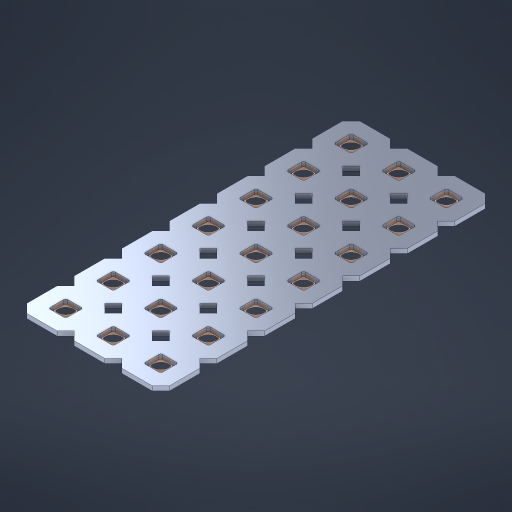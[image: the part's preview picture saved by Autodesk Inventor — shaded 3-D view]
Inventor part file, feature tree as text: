
AUTODESK INVENTOR PART (.ipt)
format: ipt  version: 2023 (Build 270158000, 158)  size: 497,664 bytes
history: native  units: in
note: dims shown in document units (in); Inventor stores cm internally (conversion verified against a paired STEP export)
features: other x22, extrude x20, sketch x2, pattern_linear x1
ambient origin geometry x8: Origin, YZ Plane, XZ Plane, XY Plane, X Axis, Y Axis, Z Axis, Center Point
bodies: Solid1 (feature_tree), Body (feature_tree)
feature tree (45):
  pattern_linear  "Rectangular Pattern1"  Spacing1=0.09in  [1 undecoded]
  sketch  "Sketch1"  dims[d1=0.5in]
  sketch  "Sketch2"  dims[d2=0.182in d3=0.09in d4=0.09in d5=0.09in d6=0.09in d7=0.09in d8=0.09in d9=0.09in d10=0.09in d11=0.02in d13=0.0in d14=0.172in d15=0.0625in d16=0.0in d19=0.5in d22=0.5in]
  other  "Srf1"
  other  "Srf126"
  other  "Srf127"
  other  "Srf128"
  other  "Srf129"
  other  "Srf130"
  other  "Srf131"
  other  "Srf268"
  other  "Srf269"
  other  "Srf270"
  other  "Srf271"
  other  "Srf272"
  other  "Srf273"
  other  "Srf274"
  other  "Srf293"
  other  "Srf294"
  other  "Srf295"
  other  "Srf296"
  other  "Srf297"
  other  "Srf298"
  other  "Srf299"
  other  "Circle"
  extrude  "ExtrusionSrf126"  Depth=0.09in
  extrude  "ExtrusionSrf127"  Depth=0.09in
  extrude  "ExtrusionSrf128"  Depth=0.09in
  extrude  "ExtrusionSrf129"  Depth=0.09in
  extrude  "ExtrusionSrf130"  Depth=0.09in
  extrude  "ExtrusionSrf131"  Depth=0.09in
  extrude  "ExtrusionSrf268"  Depth=0.09in
  extrude  "ExtrusionSrf269"  Depth=0.02in
  extrude  "ExtrusionSrf270"  TaperAngle=0.0deg  [1 undecoded]
  extrude  "ExtrusionSrf271"  Depth=0.5in
  extrude  "ExtrusionSrf272"  Depth=0.5in TaperAngle=0.0deg
  extrude  "ExtrusionSrf273"  Depth=0.5in
  extrude  "ExtrusionSrf274"  Depth=0.5in
  extrude  "ExtrusionSrf293"  [1 undecoded]
  extrude  "ExtrusionSrf294"  [1 undecoded]
  extrude  "ExtrusionSrf295"  [1 undecoded]
  extrude  "ExtrusionSrf296"  [1 undecoded]
  extrude  "ExtrusionSrf297"  [1 undecoded]
  extrude  "ExtrusionSrf298"  [1 undecoded]
  extrude  "ExtrusionSrf299"  [1 undecoded]
note: 9 required parameter values undecoded (feature->parameter linkage not recoverable at this tier; creation-order binding heuristic only, values carry confidence <= 0.55)
